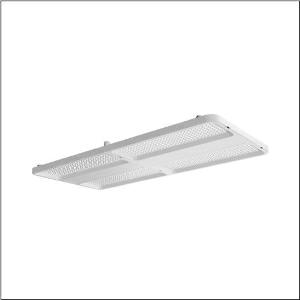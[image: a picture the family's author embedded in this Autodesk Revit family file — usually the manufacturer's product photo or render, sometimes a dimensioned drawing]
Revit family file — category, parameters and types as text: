
# Revit family: highbay_21_maxi_52hn11db4tda
name_source: partatom
category: Lighting Fixtures
units: mm (PartAtom-declared; Revit-internal decimal feet)

## family parameters
Cut with Voids When Loaded = No
Host = Face
Light Source = No
Part Type = Normal
Room Calculation Point = No
Round Connector Dimension = Use Diameter
Shared = No

## types (1)
- --- (1 x LED, 8350 lm, 44.8 W, 4000K)
    Apparent Load = 45 VA
    CIE Flux Codes = 89 97 99 100 100
    Color Rendering = 80
    Color Temperature = 4000K
    Default Elevation = 1800 mm
    Description = high bay luminaire Highbay 21 maxi; direct symmetric narrow distribution, light control with lens of PMMA; UGR ≤ 22 (X = 4H | Y = 8H | S = 0.25H | reflection values 70/50/20); luminous flux: 53.000lm; light colour: 840, colour temperature: 4000K, MacAdam ≤ 3 SDCM (initial), colour rendering: CRI > 80; luminous efficacy: 184,9lm/W; rated service life: 75.000h (L80) at AT= ta max; control: DALI 2; luminaire connection: terminal, 5-pole, max. 2.5mm² (cable entry for one cable, Ø 8.5..16mm); mains connection: 230..240V, AC/DC 0/50..60Hz; connected load: 286,6W; protection rating (complete): IP66; insulation class (complete): insulation class I (protective earthing); protection symbol: D; impact resistance: IK08; certification: CE, ENEC, VDE, UKCA; luminaire for central battery installations according to EN 60598-2-22, internal wiring halogen-free; luminaire LABS conformity tested according to VDMA 24364:2018-05; Suitable for use in the food industry according to the specifications of IFS-Food, HACCP and/or BRC; housing frame of high-performance plastic PA6, matt traffic white (RAL 9016); cover of PMMA; dimension (LxWxH): 946 x 442 x 72mm; permissible operating ambient temperature: -40..+55°C (reducing of maximum allowable ambient temperature of 5°C with ceiling mounting); packaging unit: 1 piece; (delivery without accessories; please order mounting accessories separately)
    Height = 72 mm  [stored 0.23622 ft]
    Lamp = 1 x LED
    Lamp Light Flux = 8350 lm
    Lamp Power = 44.8 W
    Lamp count = 1
    Length = 946 mm
    Luminous efficacy = 186 lm/W
    Manufacturer = Siteco
    ModVariant = No
    Model = 52HN11DB4TDA
    Mounting Place = Ceiling
    Mounting Type = Pendant
    Number of Poles = 1
    OnlyDefault = Yes
    Power Factor = 1
    Product Name = Highbay 21 maxi
    Product group = high bay luminaire
    ProductGroupID = 902
    Protection Class = Protection class I
    Protection Degree = IP 66
    RLX_Detail_Level = 1
    RLX_Emergency_Light_Flux = 0 lm
    RLX_Emergency_Type = 0
    RLX_Emergency_Type_DB = No
    RlxData = <blob elided: 127945 chars, md5=2628fc77>
    Socket = socket
    Standby Power = 0 W
    System Light Flux = 8350 lm
    System Power = 45 W
    Type Comments = : DC mode (central or group accumulator) initial emergency light level
    Type Image = l_1363244.jpg
    URL = http://relux.com
    VarID = @adj_017763
    Voltage = 0 V
    Weight = 0.00 kg
    Width = 442 mm

note: [stored X ft] marks values corroborated as IEEE doubles in the binary element streams (Revit-internal decimal feet)

## geometry (parser evidence)
native form markers: Blend x4, Sweep x11
no freeform markers — native parametric forms only
